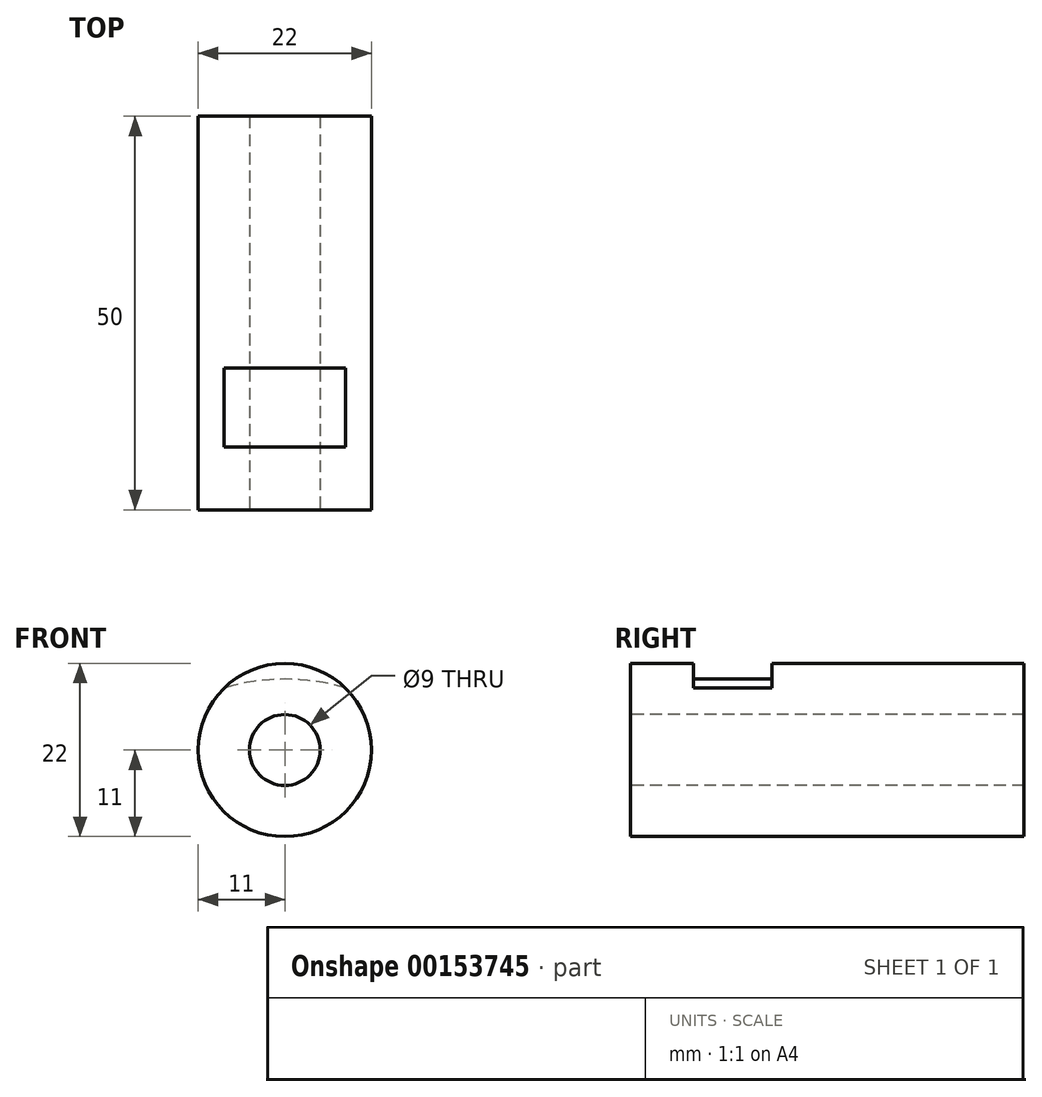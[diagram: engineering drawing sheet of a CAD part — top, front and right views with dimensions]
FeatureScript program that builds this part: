
annotation { "Feature Type Name" : "Feature", "Feature Type Description" : "" }
export const myFeature = defineFeature(function(context is Context, id is Id, definition is map)
    precondition{}
    {
        {
            var Q0;
            Q0=qCreatedBy(makeId("Front.planeOp"),FACE);
            var sketch = newSketch(context, id + "F0", { "sketchPlane" : qUnion([Q0])});
            skCircle(sketch, "E0", {"center": v(0, 0) * mm, "radius": 11 * mm});
            skCircle(sketch, "E1", {"center": v(0, 0) * mm, "radius": 4.5 * mm});
            skLineSegment(sketch, "E2", {"start": v(0, 0) * mm, "end": v(0, -17.5) * mm});
            skArc(sketch, "E3", {"start": v(7.7, 7.86) * mm, "mid": v(0, 9) * mm, "end": v(-7.7, 7.86) * mm});
            skSolve(sketch);
        }
        {
            var Q0;
            Q0 = qSketchRegion(id + "F0", true);
            extrude(context, id + "F1", {"entities" : qUnion([Q0]), "oppositeDirection" : true, "depth" : 8 * mm});
        }
        {
            var Q0;
            Q0=makeQuery(id+"F0.imprint","IMPRINT",FACE,{"disambiguationData":[TD([[makeQuery(id+"F0.imprint","IMPRINT",EDGE,{"derivedFrom":sQuery(id+"F0.wireOp",EDGE,"E1")}),-1.0]])]});
            extrude(context, id + "F2", {"entities" : qUnion([Q0]), "operationType" : NewBodyOperationType.ADD, "oppositeDirection" : true, "depth" : 18 * mm});
        }
        {
            var Q0;
            Q0=makeQuery(id+"F0.imprint","IMPRINT",FACE,{"disambiguationData":[TD([[makeQuery(id+"F0.imprint","IMPRINT",EDGE,{"derivedFrom":sQuery(id+"F0.wireOp",EDGE,"E1")}),-1.0]])]});
            var Q1;
            {var subQ0=sQuery(id+"F0.wireOp",EDGE,"E3");Q1=makeQuery(id+"F0.imprint","IMPRINT",FACE,{"disambiguationData":[TD([[makeQuery(id+"F0.imprint","IMPRINT",EDGE,{"derivedFrom":subQ0}),-1.0]])]});}
            var Q2;
            Q2=sQuery(id+"F0.wireOp",EDGE,"E0");
            var Q3;
            Q3=sQuery(id+"F0.wireOp",EDGE,"E1");
            extrude(context, id + "F3", {"entities" : qUnion([Q0, Q1]), "operationType" : NewBodyOperationType.ADD, "surfaceEntities" : qUnion([Q2, Q3]), "oppositeDirection" : true, "depth" : 50 * mm, "hasSecondDirection" : true, "secondDirectionOppositeDirection" : true, "secondDirectionDepth" : 18 * mm});
        }
    });
